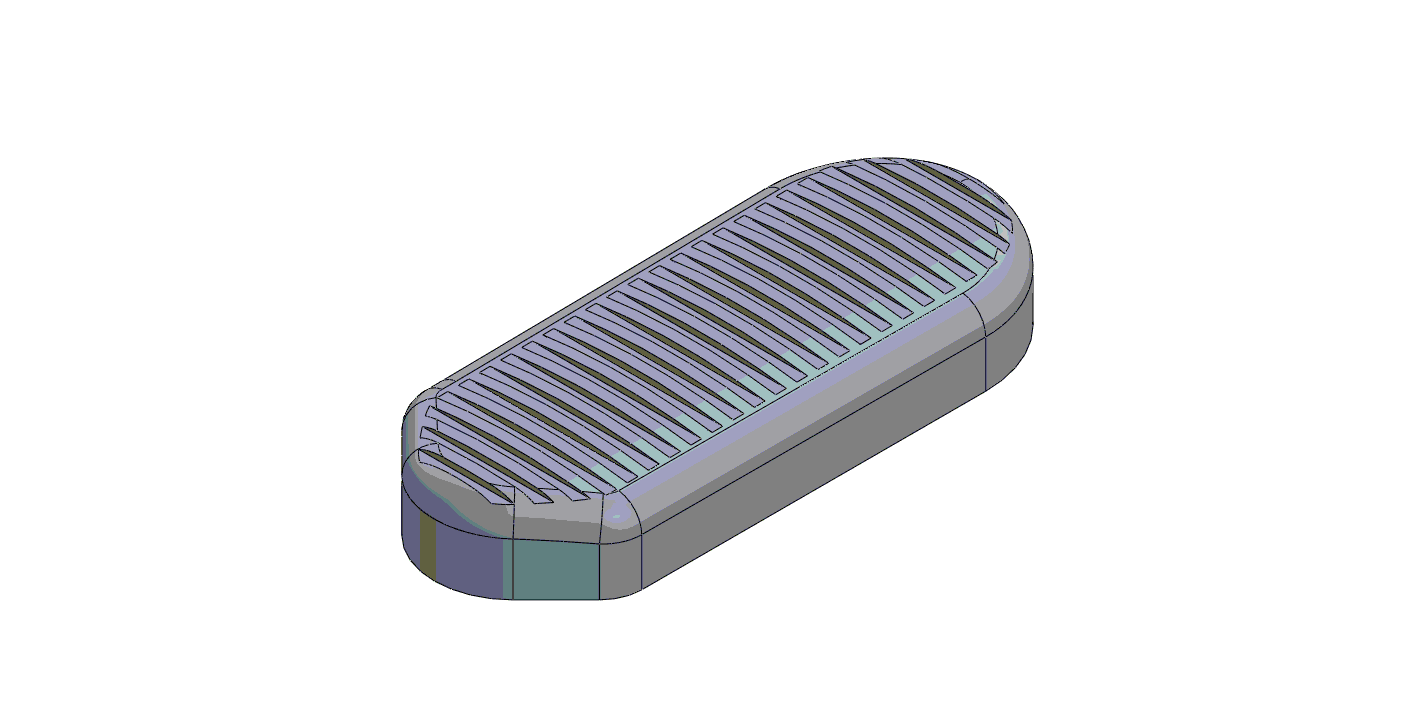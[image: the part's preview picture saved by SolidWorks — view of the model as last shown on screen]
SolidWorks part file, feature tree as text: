
SOLIDWORKS PART (.sldprt)
format: sldprt  version: not decoded by parser v0  size: 610,816 bytes
history: native  units: mm
features: sketch x10, extrude x5, cut_extrude x5, fillet x2, material x1, pattern_linear x1 (+12 scaffold rows collapsed)
feature tree (36):
  scaffold x12  (default folders/planes/origin — collapsed)
  material  "Material <not specified>"
  sketch  "Sketch1"
  extrude  "Boss-Extrude1"  Depth=10mm
  sketch  "Sketch2"
  extrude  "Boss-Extrude2"  Depth=15mm
  fillet  "Fillet1"  Radius=1.27mm
  sketch  "Sketch3"
  cut_extrude  "Cut-Extrude5"  Depth=5mm
  sketch  "Sketch4"
  extrude  "Boss-Extrude3"  [1 undecoded]
  sketch  "Sketch5"  dims[D1=0.0mm]
  extrude  "Boss-Extrude4"  Depth=12.7mm
  sketch  "3DSketch1"  dims[c1.D1=203.2mm c2.D1=101.6mm c3.D1=101.6mm c4.D1=19.05mm c5.D1=19.05mm]
  cut_extrude  "Cut-Extrude7"  Depth=101.6mm
  fillet  "Fillet5"  Radius=6.35mm
  sketch  "Sketch6"  dims[D1=~13.297786mm]
  cut_extrude  "Cut-Extrude9"  Depth=10mm
  sketch  "Sketch7"
  extrude  "Boss-Extrude5"  [1 undecoded]
  sketch  "Sketch8"  dims[D1=12.7mm]
  cut_extrude  "Cut-Extrude10"  Depth=5mm
  sketch  "Sketch9"  dims[D1=2.54mm]
  cut_extrude  "Cut-Extrude11"  Depth=57.404mm
  pattern_linear  "LPattern4"  Count1=14 Count2=12 Spacing1=5.08mm Spacing2=5.08mm
decode coverage: 16 of 23 modeling features carry decoded parameters
note: ~ marks probable driven/reference dimensions
note: 2 parameter values undecoded
note: suppression state not decoded; provenance and decode notes live in map.json
